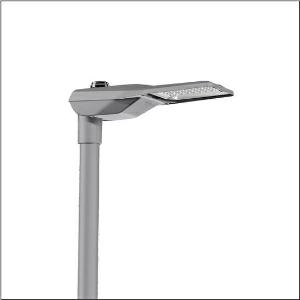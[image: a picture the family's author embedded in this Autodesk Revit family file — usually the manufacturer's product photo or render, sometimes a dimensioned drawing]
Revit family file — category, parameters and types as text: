
# Revit family: streetlight_sl_21_mini___pl52_5xe6h37n08hb_79bc
name_source: partatom
category: Lighting Fixtures
units: mm (PartAtom-declared; Revit-internal decimal feet)

## family parameters
Cut with Voids When Loaded = No
Host = Face
Light Source = No
Part Type = Normal
Room Calculation Point = No
Round Connector Dimension = Use Diameter
Shared = No

## types (1)
- --- (1 x LED, 8890 lm, 66 W, 3000K)
    Apparent Load = 66 VA
    CIE Flux Codes = 27 59 98 100 100
    Color Rendering = 70
    Color Temperature = 3000K
    Default Elevation = 1800 mm
    Description = Streetlight SL 21 mini, mast luminaire, primary light control with lens, of PMMA, primary optical cover: cover, of toughened safety glass, transparent, light distribution: PL52, light emission: direct distribution, primary light characteristic: asymmetric, installation type: side-entry, LED, 3G 1.5mm², High Power LED, rated luminous flux: 8.890lm, luminous efficacy: 135lm/W, light colour: 730, colour temperature: 3000K, control: overheat protection, pre-setting: linear dimming characteristic, constant luminous flux control, time-dependent luminous flux control, flexible luminous flux parameterisation, mains connection: 230..240V, AC, 50/60Hz, connection cable pre-assembled, cable length: 8,5m, wiring characteristics: H07RN-F, start of lifetime: 66W, end of service life: 69W, reduction: 30W, luminaire housing, of diecast aluminium (EN AC-44300), powder-coated, Siteco® metallic grey (DB 702S), corrosivity category C5 mid according to DIN EN ISO 12944, multi-level sealing system, sealing non-destructively replaceable, inclination adjustable: 0°, 5°, 10°, 15°, length: 628mm, width: 235mm, height: 110mm, spigot size: 42mm (side-entry), protection rating (complete): IP66, insulation class (complete): insulation class I (protective earthing), certification: CE, ENEC, ENEC+, VDE, impact resistance: IK09, permissible operating ambient temperature for outdoor applications: -40..+50°C, standard-compliant lighting for roads and squares, packaging unit: 1 piece

Light Distribution: PL52
    Height = 110 mm
    Lamp = 1 x LED
    Lamp Light Flux = 8890 lm
    Lamp Power = 66 W
    Lamp count = 1
    Length = 625 mm
    Luminous efficacy = 135 lm/W
    Manufacturer = Siteco
    ModVariant = No
    Model = 5XE6H37N08HB
    Number of Poles = 1
    OnlyDefault = Yes
    Power Factor = 1
    Product Name = Streetlight SL 21 mini | PL52
    Product group = mast luminaire | pylon top
    ProductGroupID = 6100
    Protection Class = Protection class I
    Protection Degree = IP 66
    RLX_Detail_Level = 1
    RLX_Emergency_Light_Flux = 0 lm
    RLX_Emergency_Type = 0
    RLX_Emergency_Type_DB = No
    RlxData = <blob elided: 101581 chars, md5=abbb24a1>
    Socket = socket
    Standby Power = 0 W
    System Light Flux = 8890 lm
    System Power = 66 W
    Type Comments = factory setting: luminous flux: 100 % | dim-lin: 254 | 670 mA
    Type Image = l_1294379.jpg
    URL = http://relux.com
    VarID = @adj_106847
    Voltage = 0 V
    Weight = 0.00 kg
    Width = 234 mm

## geometry (parser evidence)
native form markers: Blend x4, Sweep x11
no freeform markers — native parametric forms only
